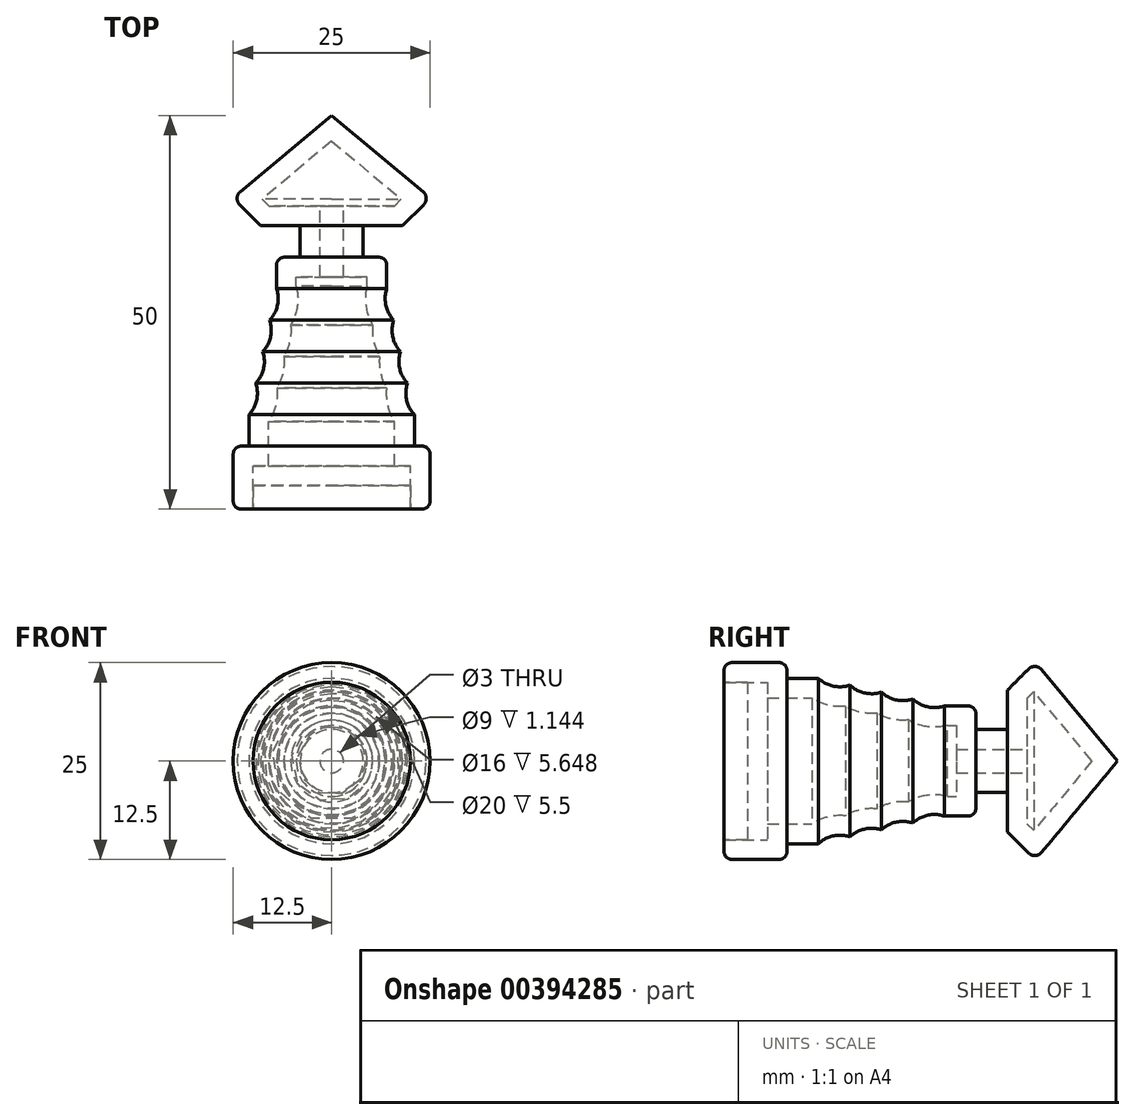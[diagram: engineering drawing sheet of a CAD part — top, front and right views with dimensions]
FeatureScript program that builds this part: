
annotation { "Feature Type Name" : "Feature", "Feature Type Description" : "" }
export const myFeature = defineFeature(function(context is Context, id is Id, definition is map)
    precondition{}
    {
        {
            var Q0;
            Q0=qCreatedBy(makeId("Top.planeOp"),FACE);
            var sketch = newSketch(context, id + "F0", { "sketchPlane" : qUnion([Q0])});
            skLineSegment(sketch, "E0", {"start": v(0, 0) * mm, "end": v(0, 58.83) * mm, "construction": true});
            skLineSegment(sketch, "E1", {"start": v(0, 58.83) * mm, "end": v(0, -63) * mm, "construction": true});
            skLineSegment(sketch, "E2", {"start": v(0, -49.5) * mm, "end": v(0, -41.5) * mm});
            skLineSegment(sketch, "E3", {"start": v(0, -41.5) * mm, "end": v(-12.5, -41.5) * mm});
            skLineSegment(sketch, "E4", {"start": v(-12.5, -41.5) * mm, "end": v(-12.5, -49.5) * mm});
            skLineSegment(sketch, "E5", {"start": v(0, -41.5) * mm, "end": v(0, -37.5) * mm});
            skLineSegment(sketch, "E6", {"start": v(0, -37.5) * mm, "end": v(-10.5, -37.5) * mm});
            skLineSegment(sketch, "E7", {"start": v(-10.5, -37.5) * mm, "end": v(-10.5, -41.5) * mm});
            skLineSegment(sketch, "E8", {"start": v(0, -37.5) * mm, "end": v(0, -33.5) * mm});
            skLineSegment(sketch, "E9", {"start": v(0, -33.5) * mm, "end": v(-9.63, -33.5) * mm});
            skArc(sketch, "E10", {"start": v(-10.5, -37.5) * mm, "mid": v(-9.52, -35.61) * mm, "end": v(-9.63, -33.5) * mm});
            skLineSegment(sketch, "E11", {"start": v(0, -49.5) * mm, "end": v(-12.5, -49.5) * mm});
            skLineSegment(sketch, "E12", {"start": v(0, -33.5) * mm, "end": v(0, -29.5) * mm});
            skLineSegment(sketch, "E13", {"start": v(0, -29.5) * mm, "end": v(-8.75, -29.5) * mm});
            skArc(sketch, "E14", {"start": v(-9.63, -33.5) * mm, "mid": v(-8.64, -31.61) * mm, "end": v(-8.75, -29.5) * mm});
            skLineSegment(sketch, "E15", {"start": v(0, -29.5) * mm, "end": v(0, -25.5) * mm});
            skLineSegment(sketch, "E16", {"start": v(0, -25.5) * mm, "end": v(-7.87, -25.5) * mm});
            skArc(sketch, "E17", {"start": v(-8.75, -29.5) * mm, "mid": v(-7.76, -27.61) * mm, "end": v(-7.87, -25.5) * mm});
            skLineSegment(sketch, "E18", {"start": v(0, -25.5) * mm, "end": v(0, -21.5) * mm});
            skLineSegment(sketch, "E19", {"start": v(0, -21.5) * mm, "end": v(-7, -21.5) * mm});
            skArc(sketch, "E20", {"start": v(-7.87, -25.5) * mm, "mid": v(-6.89, -23.61) * mm, "end": v(-7, -21.5) * mm});
            skLineSegment(sketch, "E21", {"start": v(0, -21.5) * mm, "end": v(0, -17.5) * mm});
            skLineSegment(sketch, "E22", {"start": v(0, -17.5) * mm, "end": v(-7, -17.5) * mm});
            skLineSegment(sketch, "E23", {"start": v(-7, -17.5) * mm, "end": v(-7, -21.5) * mm});
            skLineSegment(sketch, "E24", {"start": v(0, -17.5) * mm, "end": v(0, -13.5) * mm});
            skLineSegment(sketch, "E25", {"start": v(0, -13.5) * mm, "end": v(-4, -13.5) * mm});
            skLineSegment(sketch, "E26", {"start": v(-4, -13.5) * mm, "end": v(-4, -17.5) * mm});
            skLineSegment(sketch, "E27", {"start": v(0, -13.5) * mm, "end": v(0, -10.5) * mm});
            skLineSegment(sketch, "E28", {"start": v(0, -10.5) * mm, "end": v(-12, -10.5) * mm});
            skLineSegment(sketch, "E29", {"start": v(-4, -13.5) * mm, "end": v(-9, -13.5) * mm});
            skLineSegment(sketch, "E30", {"start": v(-12, -10.5) * mm, "end": v(-9, -13.5) * mm});
            skLineSegment(sketch, "E31", {"start": v(-12, -10.5) * mm, "end": v(-12, -9.5) * mm});
            skLineSegment(sketch, "E32", {"start": v(-12, -9.5) * mm, "end": v(0, 0.5) * mm});
            skLineSegment(sketch, "E33", {"start": v(0, 0.5) * mm, "end": v(0, -10.5) * mm});
            skSolve(sketch);
        }
        {
            var Q0;
            Q0 = qSketchRegion(id + "F0", true);
            var Q1;
            Q1=sQuery(id+"F0.wireOp",EDGE,"E1");
            revolve(context, id + "F1", {"entities" : qUnion([Q0]), "axis" : qUnion([Q1]), "revolveType" : RevolveType.FULL});
        }
        {
            var Q0;
            Q0=makeQuery(id+"F1.opRevolve","SWEPT_EDGE",EDGE,{"disambiguationData":[OSD([sQuery(id+"F0.wireOp",EDGE,"E28"),sQuery(id+"F0.wireOp",EDGE,"E30"),sQuery(id+"F0.wireOp",EDGE,"E31")])]});
            var Q1;
            Q1=makeQuery(id+"F1.opRevolve","SWEPT_EDGE",EDGE,{"disambiguationData":[OSD([sQuery(id+"F0.wireOp",EDGE,"E31"),sQuery(id+"F0.wireOp",EDGE,"E32")])]});
            fillet(context, id + "F2", {"entities" : qUnion([Q0, Q1]), "radius" : 1 * mm, "tangentPropagation" : true, "allowEdgeOverflow" : false});
        }
        {
            var Q0;
            Q0=makeQuery(id+"F1.opRevolve","SWEPT_EDGE",EDGE,{"disambiguationData":[OSD([sQuery(id+"F0.wireOp",EDGE,"E22"),sQuery(id+"F0.wireOp",EDGE,"E23")])]});
            fillet(context, id + "F3", {"entities" : qUnion([Q0]), "radius" : 1 * mm, "tangentPropagation" : true, "allowEdgeOverflow" : false});
        }
        {
            var Q0;
            Q0=makeQuery(id+"F1.opRevolve","SWEPT_EDGE",EDGE,{"disambiguationData":[OSD([sQuery(id+"F0.wireOp",EDGE,"E3"),sQuery(id+"F0.wireOp",EDGE,"E4")])]});
            var Q1;
            Q1=makeQuery(id+"F1.opRevolve","SWEPT_FACE",FACE,{"disambiguationData":[OSD([sQuery(id+"F0.wireOp",EDGE,"E4")])]});
            fillet(context, id + "F4", {"entities" : qUnion([Q0, Q1]), "radius" : 1 * mm, "tangentPropagation" : true, "allowEdgeOverflow" : false});
        }
        {
            var Q0;
            Q0=makeQuery(id+"F1.opRevolve","SWEPT_FACE",FACE,{"disambiguationData":[OSD([sQuery(id+"F0.wireOp",EDGE,"E11")])]});
            shell(context, id + "F5", {"entities" : qUnion([Q0]), "thickness" : 2.5 * mm});
        }
        {
            var Q0;
            Q0=makeQuery(id+"F1.opRevolve","SWEPT_FACE",FACE,{"disambiguationData":[OSD([sQuery(id+"F0.wireOp",EDGE,"E11")])]});
            var sketch = newSketch(context, id + "F6", { "sketchPlane" : qUnion([Q0])});
            skCircle(sketch, "E34", {"center": v(0, 0) * mm, "radius": 10 * mm});
            skSolve(sketch);
        }
        {
            var Q0;
            Q0 = qSketchRegion(id + "F6", true);
            extrude(context, id + "F7", {"entities" : qUnion([Q0]), "oppositeDirection" : true, "depth" : 3 * mm});
        }
    });
